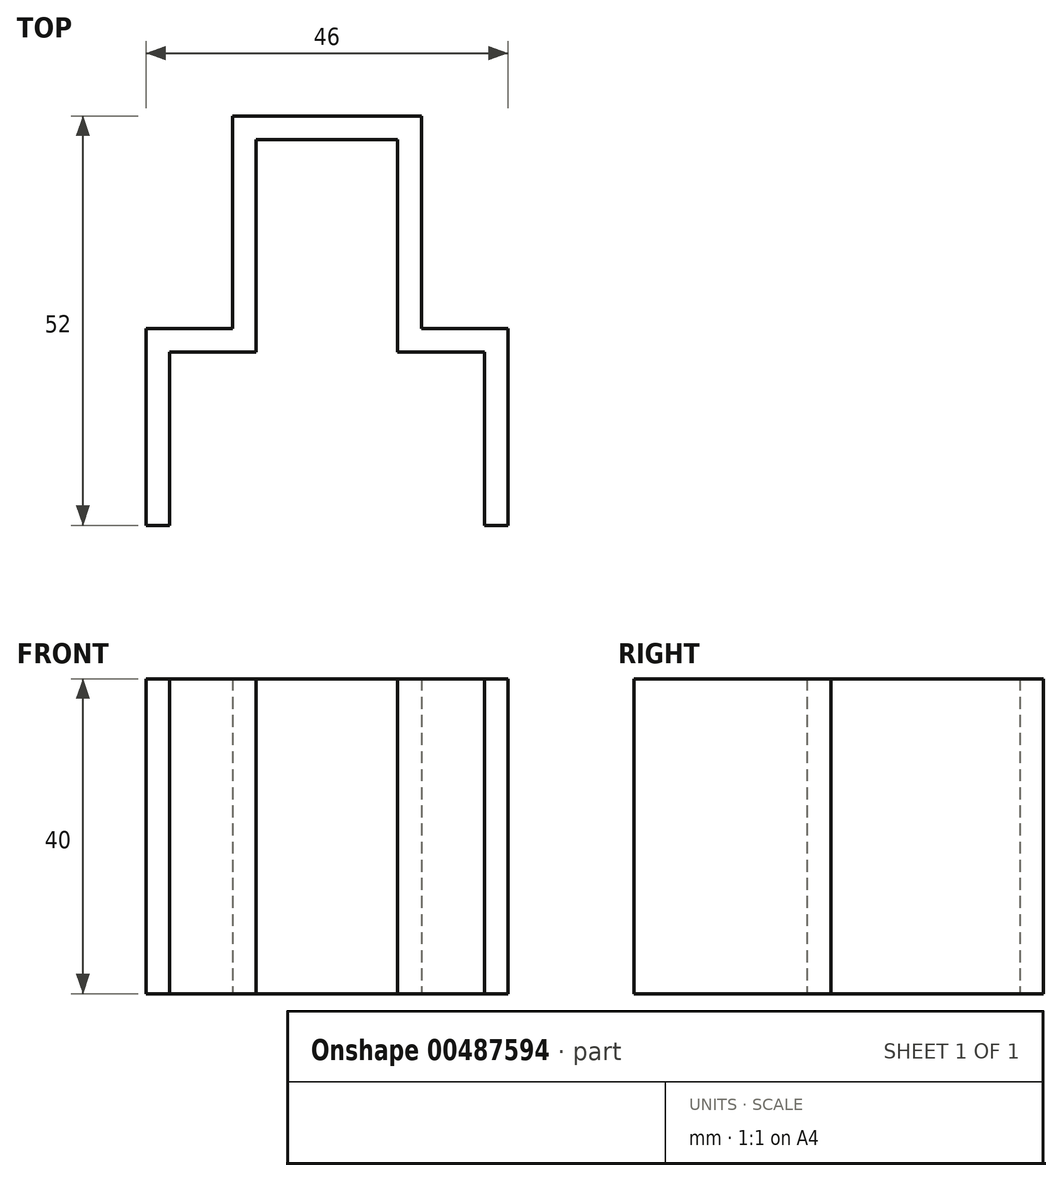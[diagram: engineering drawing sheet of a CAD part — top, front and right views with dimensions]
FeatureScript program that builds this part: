
annotation { "Feature Type Name" : "Feature", "Feature Type Description" : "" }
export const myFeature = defineFeature(function(context is Context, id is Id, definition is map)
    precondition{}
    {
        {
            var Q0;
            Q0=qCreatedBy(makeId("Top.planeOp"),FACE);
            var sketch = newSketch(context, id + "F0", { "sketchPlane" : qUnion([Q0])});
            skLineSegment(sketch, "E0", {"start": v(0, 14) * mm, "end": v(-9, 14) * mm});
            skLineSegment(sketch, "E1", {"start": v(-9, 14) * mm, "end": v(-9, -13) * mm});
            skLineSegment(sketch, "E2", {"start": v(-9, -13) * mm, "end": v(-20, -13) * mm});
            skLineSegment(sketch, "E3", {"start": v(-20, -13) * mm, "end": v(-20, -35) * mm});
            skLineSegment(sketch, "E4", {"start": v(0, 17) * mm, "end": v(-12, 17) * mm});
            skLineSegment(sketch, "E5", {"start": v(-12, 17) * mm, "end": v(-12, -10) * mm});
            skLineSegment(sketch, "E6", {"start": v(-12, -10) * mm, "end": v(-23, -10) * mm});
            skLineSegment(sketch, "E7", {"start": v(-23, -10) * mm, "end": v(-23, -35) * mm});
            skLineSegment(sketch, "E8", {"start": v(-23, -35) * mm, "end": v(-20, -35) * mm});
            skLineSegment(sketch, "E9.MirrorCS", {"start": v(23, -35) * mm, "end": v(20, -35) * mm});
            skLineSegment(sketch, "E10.MirrorCS", {"start": v(9, -13) * mm, "end": v(20, -13) * mm});
            skLineSegment(sketch, "E11.MirrorCS", {"start": v(12, 17) * mm, "end": v(12, -10) * mm});
            skLineSegment(sketch, "E12.MirrorCS", {"start": v(12, -10) * mm, "end": v(23, -10) * mm});
            skLineSegment(sketch, "E13.MirrorCS", {"start": v(23, -10) * mm, "end": v(23, -35) * mm});
            skLineSegment(sketch, "E14.MirrorCS", {"start": v(9, 14) * mm, "end": v(9, -13) * mm});
            skLineSegment(sketch, "E15.MirrorCS", {"start": v(0, 14) * mm, "end": v(9, 14) * mm});
            skLineSegment(sketch, "E16.MirrorCS", {"start": v(0, 17) * mm, "end": v(12, 17) * mm});
            skLineSegment(sketch, "E17.MirrorCS", {"start": v(20, -13) * mm, "end": v(20, -35) * mm});
            skSolve(sketch);
        }
        {
            var Q0;
            Q0=qSketchRegion(id+"F0",true);
            extrude(context, id + "F1", {"entities" : qUnion([Q0]), "depth" : 40 * mm});
        }
    });
